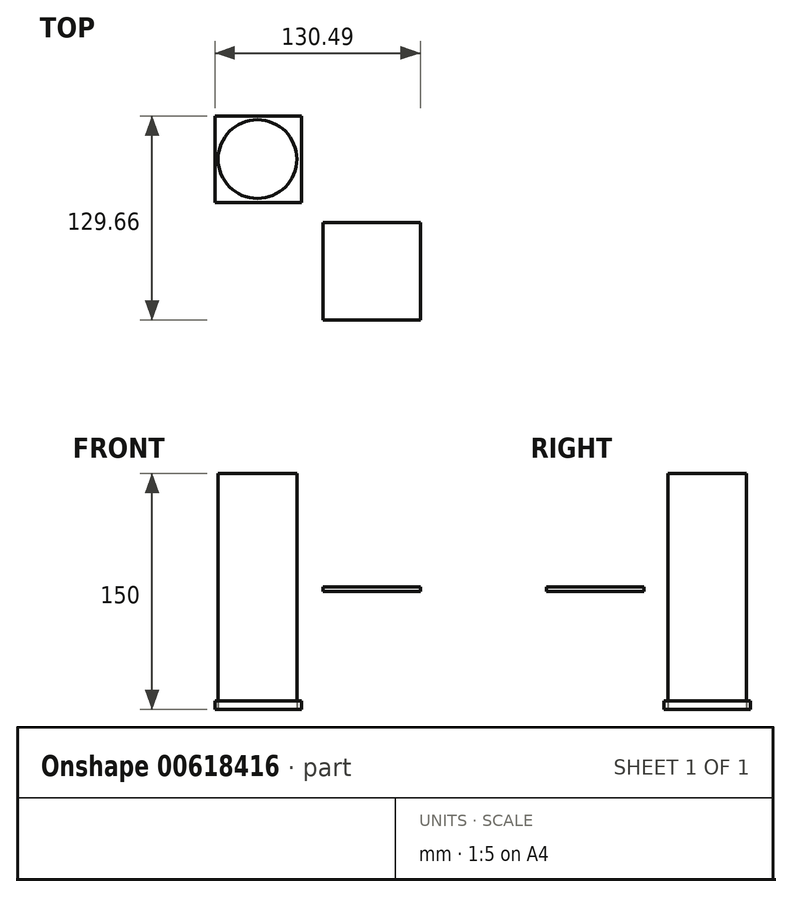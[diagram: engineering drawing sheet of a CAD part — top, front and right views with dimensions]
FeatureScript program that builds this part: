
annotation { "Feature Type Name" : "Feature", "Feature Type Description" : "" }
export const myFeature = defineFeature(function(context is Context, id is Id, definition is map)
    precondition{}
    {
        {
            var Q0;
            Q0=qCreatedBy(makeId("Top.planeOp"),FACE);
            var sketch = newSketch(context, id + "F0", { "sketchPlane" : qUnion([Q0])});
            skCircle(sketch, "E0", {"center": v(0, 0) * mm, "radius": 25 * mm});
            skSolve(sketch);
        }
        {
            var Q0;
            Q0=makeQuery(id+"F0.imprint","IMPRINT",FACE,{"disambiguationData":[TD([[makeQuery(id+"F0.imprint","IMPRINT",EDGE,{"derivedFrom":sQuery(id+"F0.wireOp",EDGE,"E0")}),1.0]])]});
            extrude(context, id + "F1", {"entities" : qUnion([Q0]), "endBound" : BoundingType.SYMMETRIC, "depth" : 150 * mm, "offsetDistance" : 25 * mm});
        }
        {
            var Q0;
            Q0=qCreatedBy(makeId("Top.planeOp"),FACE);
            var sketch = newSketch(context, id + "F2", { "sketchPlane" : qUnion([Q0])});
            skLineSegment(sketch, "E1.bottom", {"start": v(27.5, 27.5) * mm, "end": v(-27.5, 27.5) * mm});
            skLineSegment(sketch, "E1.top", {"start": v(27.5, -27.5) * mm, "end": v(-27.5, -27.5) * mm});
            skLineSegment(sketch, "E1.left", {"start": v(27.5, 27.5) * mm, "end": v(27.5, -27.5) * mm});
            skLineSegment(sketch, "E1.right", {"start": v(-27.5, 27.5) * mm, "end": v(-27.5, -27.5) * mm});
            skPoint(sketch, "E1.middle", {"position": v(0, 0) * mm});
            skSolve(sketch);
        }
        {
            var Q0;
            Q0=makeQuery(id+"F2.imprint","IMPRINT",FACE,{"disambiguationData":[TD([[makeQuery(id+"F2.imprint","IMPRINT",EDGE,{"derivedFrom":sQuery(id+"F2.wireOp",EDGE,"E1.bottom")}),1.0]])]});
            extrude(context, id + "F3", {"entities" : qUnion([Q0]), "depth" : 5.4 * mm, "offsetDistance" : 25 * mm});
        }
        {
            var Q0;
            Q0=makeQuery(id+"F3.opExtrude","SWEPT_BODY",BODY,{"disambiguationData":[OSD([sQuery(id+"F2.wireOp",EDGE,"E1.bottom"),sQuery(id+"F2.wireOp",EDGE,"E1.top"),sQuery(id+"F2.wireOp",EDGE,"E1.left"),sQuery(id+"F2.wireOp",EDGE,"E1.right")])]});
            transform(context, id + "F4", {"entities" : qUnion([Q0]), "transformType" : TransformType.TRANSLATION_3D, "dx" : 0.5 * mm, "dy" : 0 * mm, "dz" : -75 * mm, "makeCopy" : false});
        }
        {
            var Q0;
            Q0=qCreatedBy(makeId("Top.planeOp"),FACE);
            var sketch = newSketch(context, id + "F5", { "sketchPlane" : qUnion([Q0])});
            skLineSegment(sketch, "E2.bottom", {"start": v(103.5, -40.16) * mm, "end": v(41.5, -40.16) * mm});
            skLineSegment(sketch, "E2.top", {"start": v(103.5, -102.16) * mm, "end": v(41.5, -102.16) * mm});
            skLineSegment(sketch, "E2.left", {"start": v(103.5, -40.16) * mm, "end": v(103.5, -102.16) * mm});
            skLineSegment(sketch, "E2.right", {"start": v(41.5, -40.16) * mm, "end": v(41.5, -102.16) * mm});
            skPoint(sketch, "E2.middle", {"position": v(72.5, -71.16) * mm});
            skSolve(sketch);
        }
        {
            var Q0;
            Q0 = qSketchRegion(id + "F5", true);
            var Q1;
            Q1=makeQuery(id+"F5.imprint","IMPRINT",FACE,{"disambiguationData":[TD([[makeQuery(id+"F5.imprint","IMPRINT",EDGE,{"derivedFrom":sQuery(id+"F5.wireOp",EDGE,"E2.bottom")}),1.0]])]});
            extrude(context, id + "F6", {"entities" : qUnion([Q0, Q1]), "depth" : 3 * mm, "offsetDistance" : 25 * mm});
        }
    });
